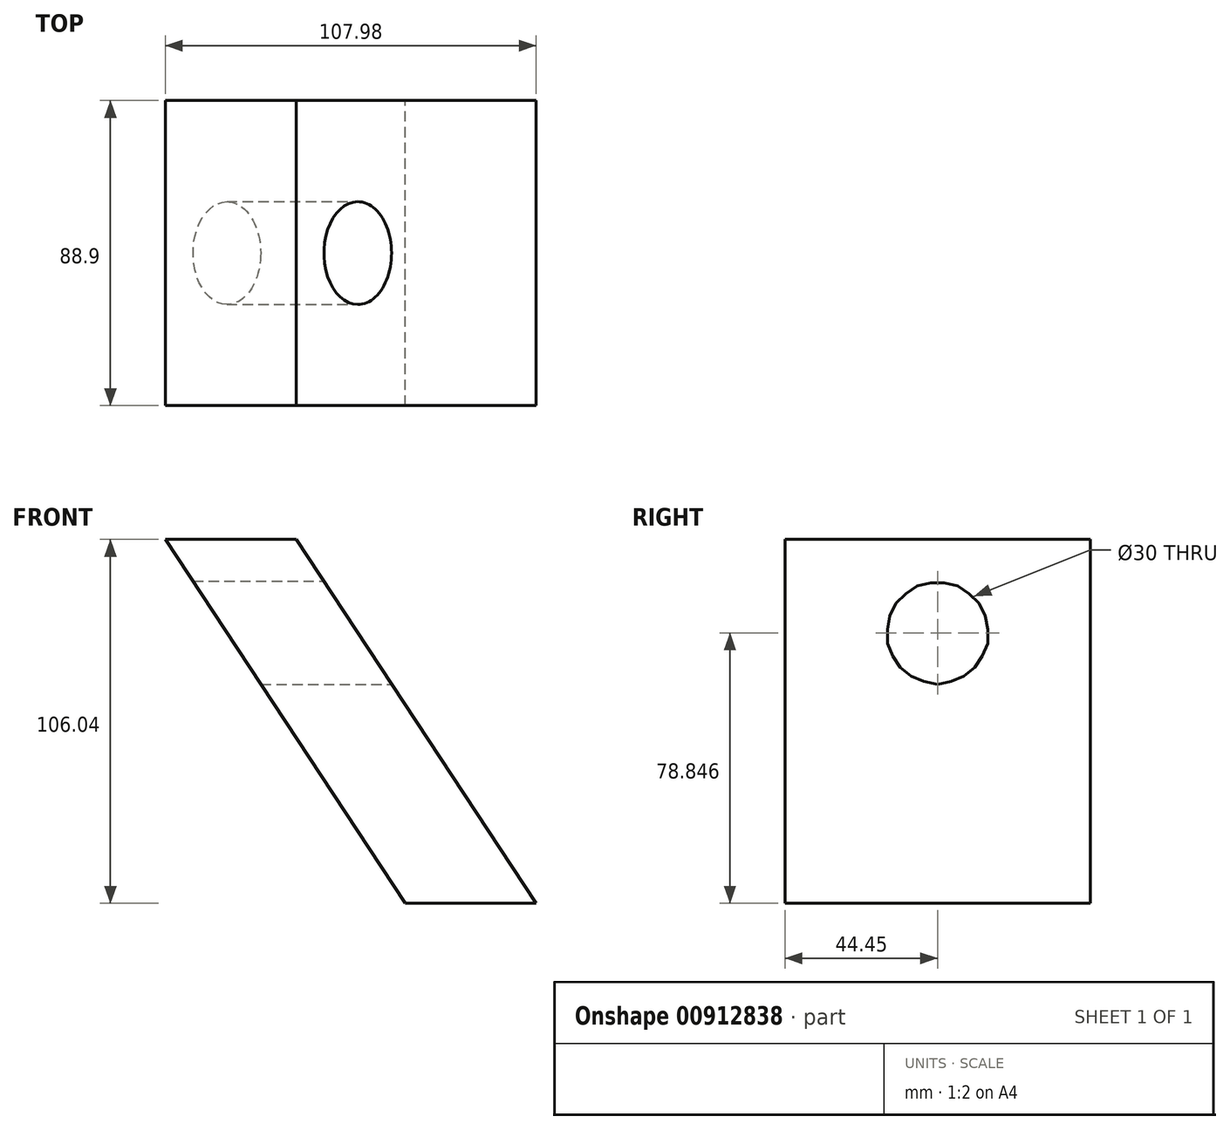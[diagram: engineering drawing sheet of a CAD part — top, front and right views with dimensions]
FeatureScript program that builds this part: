
annotation { "Feature Type Name" : "Feature", "Feature Type Description" : "" }
export const myFeature = defineFeature(function(context is Context, id is Id, definition is map)
    precondition{}
    {
        {
            var Q0;
            Q0=qCreatedBy(makeId("Front.planeOp"),FACE);
            var sketch = newSketch(context, id + "F0", { "sketchPlane" : qUnion([Q0])});
            skLineSegment(sketch, "E0", {"start": v(0, 0) * mm, "end": v(-38.1, 0) * mm});
            skLineSegment(sketch, "E1", {"start": v(-38.1, 0) * mm, "end": v(-107.98, 106.04) * mm});
            skLineSegment(sketch, "E2", {"start": v(-107.98, 106.04) * mm, "end": v(-69.88, 106.04) * mm});
            skLineSegment(sketch, "E3", {"start": v(-69.88, 106.04) * mm, "end": v(0, 0) * mm});
            skSolve(sketch);
        }
        {
            var Q0;
            Q0=makeQuery(id+"F0.imprint","IMPRINT",FACE,{"disambiguationData":[TD([[makeQuery(id+"F0.imprint","IMPRINT",EDGE,{"derivedFrom":sQuery(id+"F0.wireOp",EDGE,"E0")}),-1.0]])]});
            extrude(context, id + "F1", {"entities" : qUnion([Q0]), "depth" : 88.9 * mm, "offsetDistance" : 25.4 * mm});
        }
        {
            var Q0;
            Q0=qCreatedBy(makeId("Right.planeOp"),FACE);
            var sketch = newSketch(context, id + "F2", { "sketchPlane" : qUnion([Q0])});
            skLineSegment(sketch, "E4.0", {"start": v(-88.9, 106.04) * mm, "end": v(0, 106.04) * mm, "construction": true});
            skLineSegment(sketch, "E5.0", {"start": v(-88.9, 106.04) * mm, "end": v(-88.9, 0) * mm, "construction": true});
            skLineSegment(sketch, "E6.0", {"start": v(0, 106.04) * mm, "end": v(0, 0) * mm, "construction": true});
            skLineSegment(sketch, "E7.0", {"start": v(-88.9, 0) * mm, "end": v(0, 0) * mm, "construction": true});
            skCircle(sketch, "E8", {"center": v(-44.45, 78.85) * mm, "radius": 15 * mm});
            skPoint(sketch, "E8.centerSnap0", {"position": v(-44.45, 106.04) * mm});
            skSolve(sketch);
        }
        {
            var Q0;
            Q0=makeQuery(id+"F2.imprint","IMPRINT",FACE,{"disambiguationData":[TD([[makeQuery(id+"F2.imprint","IMPRINT",EDGE,{"derivedFrom":sQuery(id+"F2.wireOp",EDGE,"E8")}),1.0]])]});
            extrude(context, id + "F3", {"entities" : qUnion([Q0]), "operationType" : NewBodyOperationType.REMOVE, "endBound" : BoundingType.THROUGH_ALL, "oppositeDirection" : true, "depth" : 25.4 * mm, "offsetDistance" : 25.4 * mm});
        }
    });
